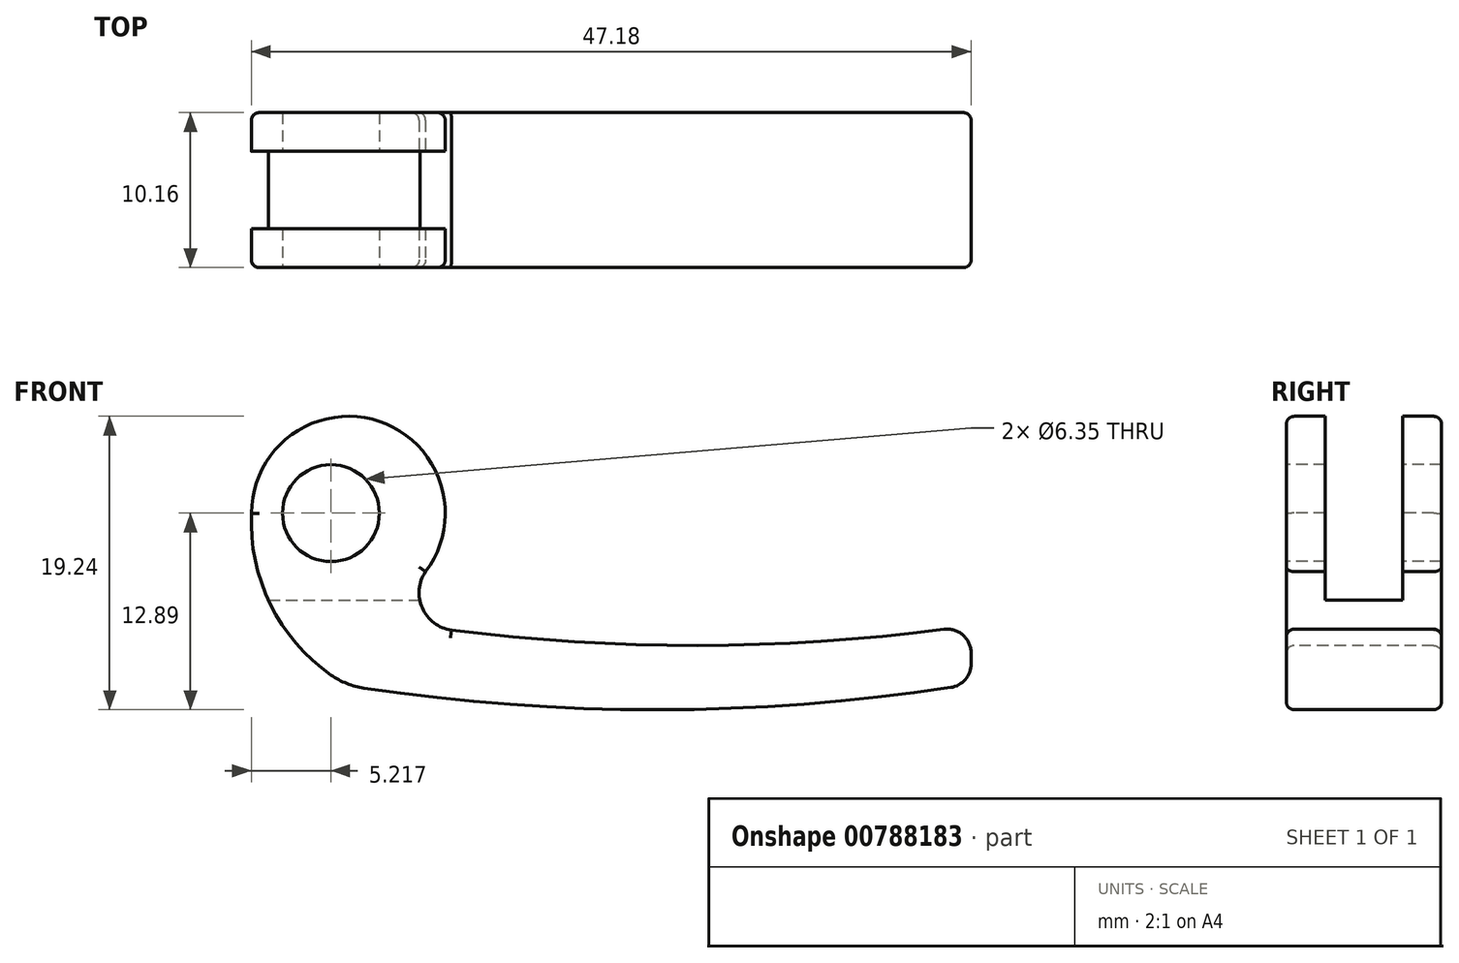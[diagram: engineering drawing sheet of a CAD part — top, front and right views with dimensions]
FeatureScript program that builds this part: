
annotation { "Feature Type Name" : "Feature", "Feature Type Description" : "" }
export const myFeature = defineFeature(function(context is Context, id is Id, definition is map)
    precondition{}
    {
        {
            var Q0;
            Q0=qCreatedBy(makeId("Front.planeOp"),FACE);
            var sketch = newSketch(context, id + "F0", { "sketchPlane" : qUnion([Q0])});
            skArc(sketch, "E0", {"start": v(5.06, -3.84) * mm, "mid": v(2.02, 6.02) * mm, "end": v(-6.35, 0) * mm});
            skCircle(sketch, "E1", {"center": v(-1.14, 0) * mm, "radius": 3.18 * mm});
            skArc(sketch, "E2", {"start": v(0, -11.31) * mm, "mid": v(20.42, -12.89) * mm, "end": v(40.82, -11.22) * mm});
            skArc(sketch, "E3", {"start": v(5.06, -3.84) * mm, "mid": v(4.85, -6.22) * mm, "end": v(6.76, -7.66) * mm});
            skLineSegment(sketch, "E4", {"start": v(40.82, -11.22) * mm, "end": v(40.82, -7.36) * mm});
            skArc(sketch, "E5", {"start": v(-6.35, 0) * mm, "mid": v(-4.8, -6.57) * mm, "end": v(0, -11.31) * mm});
            skPoint(sketch, "E6.end.orphan", {"position": v(-7.62, -12.7) * mm});
            skArc(sketch, "E7.trimOffspring", {"start": v(6.76, -7.66) * mm, "mid": v(23.8, -8.67) * mm, "end": v(40.82, -7.36) * mm});
            skSolve(sketch);
        }
        {
            var Q0;
            Q0=qSketchRegion(id+"F0",true);
            extrude(context, id + "F1", {"entities" : qUnion([Q0]), "oppositeDirection" : true, "depth" : 10.16 * mm});
        }
        {
            var Q0;
            Q0=makeQuery(id+"F1.opExtrude","SWEPT_EDGE",EDGE,{"disambiguationData":[OSD([sQuery(id+"F0.wireOp",EDGE,"E4"),sQuery(id+"F0.wireOp",EDGE,"E7.trimOffspring")])]});
            var Q1;
            Q1=makeQuery(id+"F1.opExtrude","SWEPT_EDGE",EDGE,{"disambiguationData":[OSD([sQuery(id+"F0.wireOp",EDGE,"E2"),sQuery(id+"F0.wireOp",EDGE,"E4")])]});
            fillet(context, id + "F2", {"entities" : qUnion([Q0, Q1]), "radius" : 1.57 * mm, "tangentPropagation" : true, "allowEdgeOverflow" : false});
        }
        {
            var Q0;
            Q0=makeQuery(id+"F1.opExtrude","SWEPT_EDGE",EDGE,{"disambiguationData":[OSD([sQuery(id+"F0.wireOp",EDGE,"E2"),sQuery(id+"F0.wireOp",EDGE,"E5")])]});
            fillet(context, id + "F3", {"entities" : qUnion([Q0]), "radius" : 5.08 * mm, "tangentPropagation" : true, "allowEdgeOverflow" : false});
        }
        {
            var Q0;
            Q0=qCreatedBy(makeId("Right.planeOp"),FACE);
            var sketch = newSketch(context, id + "F4", { "sketchPlane" : qUnion([Q0])});
            skLineSegment(sketch, "E8.bottom", {"start": v(2.54, 7.62) * mm, "end": v(7.62, 7.62) * mm});
            skLineSegment(sketch, "E8.top", {"start": v(2.54, -5.72) * mm, "end": v(7.62, -5.72) * mm});
            skLineSegment(sketch, "E8.left", {"start": v(2.54, 7.62) * mm, "end": v(2.54, -5.72) * mm});
            skLineSegment(sketch, "E8.right", {"start": v(7.62, 7.62) * mm, "end": v(7.62, -5.72) * mm});
            skSolve(sketch);
        }
        {
            var Q0;
            Q0=qSketchRegion(id+"F4",true);
            extrude(context, id + "F5", {"entities" : qUnion([Q0]), "operationType" : NewBodyOperationType.REMOVE, "endBound" : BoundingType.SYMMETRIC, "oppositeDirection" : true, "depth" : 25.4 * mm});
        }
        {
            var Q0;
            Q0=makeQuery(id+"F1.opExtrude","CAP_EDGE",EDGE,{"disambiguationData":[OSD([sQuery(id+"F0.wireOp",EDGE,"E0")])],"isStart":true});
            var Q1;
            Q1=makeQuery(id+"F1.opExtrude","CAP_EDGE",EDGE,{"disambiguationData":[OSD([sQuery(id+"F0.wireOp",EDGE,"E3")])],"isStart":true});
            var Q2;
            Q2=makeQuery(id+"F1.opExtrude","CAP_EDGE",EDGE,{"disambiguationData":[OSD([sQuery(id+"F0.wireOp",EDGE,"E7.trimOffspring")])],"isStart":true});
            var Q3;
            {var subQ0=sQuery(id+"F0.wireOp",EDGE,"E4");var subQ1=sQuery(id+"F0.wireOp",EDGE,"E7.trimOffspring");Q3=makeQuery(id+"F2.opFillet","BLEND_EDGE",EDGE,{"blendedFrom":[makeQuery(id+"F1.opExtrude","SWEPT_EDGE",EDGE,{"disambiguationData":[OSD([subQ0,subQ1])]}),makeQuery(id+"F1.opExtrude","CAP_FACE",FACE,{"disambiguationData":[OSD([sQuery(id+"F0.wireOp",EDGE,"E0"),sQuery(id+"F0.wireOp",EDGE,"E1"),sQuery(id+"F0.wireOp",EDGE,"E2"),sQuery(id+"F0.wireOp",EDGE,"E3"),subQ0,sQuery(id+"F0.wireOp",EDGE,"E5"),subQ1])],"isStart":true})],"blendedInto":[makeQuery(id+"F1.opExtrude","CAP_FACE",FACE,{"disambiguationData":[OSD([sQuery(id+"F0.wireOp",EDGE,"E0"),sQuery(id+"F0.wireOp",EDGE,"E1"),sQuery(id+"F0.wireOp",EDGE,"E2"),sQuery(id+"F0.wireOp",EDGE,"E3"),subQ0,sQuery(id+"F0.wireOp",EDGE,"E5"),subQ1])],"isStart":true})]});}
            var Q4;
            Q4=makeQuery(id+"F1.opExtrude","CAP_EDGE",EDGE,{"disambiguationData":[OSD([sQuery(id+"F0.wireOp",EDGE,"E4")])],"isStart":true});
            var Q5;
            {var subQ0=sQuery(id+"F0.wireOp",EDGE,"E2");var subQ1=sQuery(id+"F0.wireOp",EDGE,"E4");Q5=makeQuery(id+"F2.opFillet","BLEND_EDGE",EDGE,{"blendedFrom":[makeQuery(id+"F1.opExtrude","SWEPT_EDGE",EDGE,{"disambiguationData":[OSD([subQ0,subQ1])]}),makeQuery(id+"F1.opExtrude","CAP_FACE",FACE,{"disambiguationData":[OSD([sQuery(id+"F0.wireOp",EDGE,"E0"),sQuery(id+"F0.wireOp",EDGE,"E1"),subQ0,sQuery(id+"F0.wireOp",EDGE,"E3"),subQ1,sQuery(id+"F0.wireOp",EDGE,"E5"),sQuery(id+"F0.wireOp",EDGE,"E7.trimOffspring")])],"isStart":true})],"blendedInto":[makeQuery(id+"F1.opExtrude","CAP_FACE",FACE,{"disambiguationData":[OSD([sQuery(id+"F0.wireOp",EDGE,"E0"),sQuery(id+"F0.wireOp",EDGE,"E1"),subQ0,sQuery(id+"F0.wireOp",EDGE,"E3"),subQ1,sQuery(id+"F0.wireOp",EDGE,"E5"),sQuery(id+"F0.wireOp",EDGE,"E7.trimOffspring")])],"isStart":true})]});}
            var Q6;
            Q6=makeQuery(id+"F1.opExtrude","CAP_EDGE",EDGE,{"disambiguationData":[OSD([sQuery(id+"F0.wireOp",EDGE,"E2")])],"isStart":true});
            var Q7;
            {var subQ0=sQuery(id+"F0.wireOp",EDGE,"E2");var subQ1=sQuery(id+"F0.wireOp",EDGE,"E5");Q7=makeQuery(id+"F3.opFillet","BLEND_EDGE",EDGE,{"blendedFrom":[makeQuery(id+"F1.opExtrude","SWEPT_EDGE",EDGE,{"disambiguationData":[OSD([subQ0,subQ1])]}),makeQuery(id+"F1.opExtrude","CAP_FACE",FACE,{"disambiguationData":[OSD([sQuery(id+"F0.wireOp",EDGE,"E0"),sQuery(id+"F0.wireOp",EDGE,"E1"),subQ0,sQuery(id+"F0.wireOp",EDGE,"E3"),sQuery(id+"F0.wireOp",EDGE,"E4"),subQ1,sQuery(id+"F0.wireOp",EDGE,"E7.trimOffspring")])],"isStart":true})],"blendedInto":[makeQuery(id+"F1.opExtrude","CAP_FACE",FACE,{"disambiguationData":[OSD([sQuery(id+"F0.wireOp",EDGE,"E0"),sQuery(id+"F0.wireOp",EDGE,"E1"),subQ0,sQuery(id+"F0.wireOp",EDGE,"E3"),sQuery(id+"F0.wireOp",EDGE,"E4"),subQ1,sQuery(id+"F0.wireOp",EDGE,"E7.trimOffspring")])],"isStart":true})]});}
            var Q8;
            Q8=makeQuery(id+"F1.opExtrude","CAP_EDGE",EDGE,{"disambiguationData":[OSD([sQuery(id+"F0.wireOp",EDGE,"E5")])],"isStart":true});
            var Q9;
            Q9=makeQuery(id+"F1.opExtrude","CAP_EDGE",EDGE,{"disambiguationData":[OSD([sQuery(id+"F0.wireOp",EDGE,"E2")])],"isStart":false});
            var Q10;
            {var subQ0=sQuery(id+"F0.wireOp",EDGE,"E2");var subQ1=sQuery(id+"F0.wireOp",EDGE,"E4");Q10=makeQuery(id+"F2.opFillet","BLEND_EDGE",EDGE,{"blendedFrom":[makeQuery(id+"F1.opExtrude","SWEPT_EDGE",EDGE,{"disambiguationData":[OSD([subQ0,subQ1])]}),makeQuery(id+"F1.opExtrude","CAP_FACE",FACE,{"disambiguationData":[OSD([sQuery(id+"F0.wireOp",EDGE,"E0"),sQuery(id+"F0.wireOp",EDGE,"E1"),subQ0,sQuery(id+"F0.wireOp",EDGE,"E3"),subQ1,sQuery(id+"F0.wireOp",EDGE,"E5"),sQuery(id+"F0.wireOp",EDGE,"E7.trimOffspring")])],"isStart":false})],"blendedInto":[makeQuery(id+"F1.opExtrude","CAP_FACE",FACE,{"disambiguationData":[OSD([sQuery(id+"F0.wireOp",EDGE,"E0"),sQuery(id+"F0.wireOp",EDGE,"E1"),subQ0,sQuery(id+"F0.wireOp",EDGE,"E3"),subQ1,sQuery(id+"F0.wireOp",EDGE,"E5"),sQuery(id+"F0.wireOp",EDGE,"E7.trimOffspring")])],"isStart":false})]});}
            var Q11;
            Q11=makeQuery(id+"F1.opExtrude","CAP_EDGE",EDGE,{"disambiguationData":[OSD([sQuery(id+"F0.wireOp",EDGE,"E4")])],"isStart":false});
            var Q12;
            {var subQ0=sQuery(id+"F0.wireOp",EDGE,"E4");var subQ1=sQuery(id+"F0.wireOp",EDGE,"E7.trimOffspring");Q12=makeQuery(id+"F2.opFillet","BLEND_EDGE",EDGE,{"blendedFrom":[makeQuery(id+"F1.opExtrude","SWEPT_EDGE",EDGE,{"disambiguationData":[OSD([subQ0,subQ1])]}),makeQuery(id+"F1.opExtrude","CAP_FACE",FACE,{"disambiguationData":[OSD([sQuery(id+"F0.wireOp",EDGE,"E0"),sQuery(id+"F0.wireOp",EDGE,"E1"),sQuery(id+"F0.wireOp",EDGE,"E2"),sQuery(id+"F0.wireOp",EDGE,"E3"),subQ0,sQuery(id+"F0.wireOp",EDGE,"E5"),subQ1])],"isStart":false})],"blendedInto":[makeQuery(id+"F1.opExtrude","CAP_FACE",FACE,{"disambiguationData":[OSD([sQuery(id+"F0.wireOp",EDGE,"E0"),sQuery(id+"F0.wireOp",EDGE,"E1"),sQuery(id+"F0.wireOp",EDGE,"E2"),sQuery(id+"F0.wireOp",EDGE,"E3"),subQ0,sQuery(id+"F0.wireOp",EDGE,"E5"),subQ1])],"isStart":false})]});}
            var Q13;
            Q13=makeQuery(id+"F1.opExtrude","CAP_EDGE",EDGE,{"disambiguationData":[OSD([sQuery(id+"F0.wireOp",EDGE,"E7.trimOffspring")])],"isStart":false});
            var Q14;
            Q14=makeQuery(id+"F1.opExtrude","CAP_EDGE",EDGE,{"disambiguationData":[OSD([sQuery(id+"F0.wireOp",EDGE,"E3")])],"isStart":false});
            var Q15;
            Q15=makeQuery(id+"F1.opExtrude","CAP_EDGE",EDGE,{"disambiguationData":[OSD([sQuery(id+"F0.wireOp",EDGE,"E0")])],"isStart":false});
            var Q16;
            Q16=makeQuery(id+"F1.opExtrude","CAP_EDGE",EDGE,{"disambiguationData":[OSD([sQuery(id+"F0.wireOp",EDGE,"E5")])],"isStart":false});
            var Q17;
            {var subQ0=sQuery(id+"F0.wireOp",EDGE,"E2");var subQ1=sQuery(id+"F0.wireOp",EDGE,"E5");Q17=makeQuery(id+"F3.opFillet","BLEND_EDGE",EDGE,{"blendedFrom":[makeQuery(id+"F1.opExtrude","SWEPT_EDGE",EDGE,{"disambiguationData":[OSD([subQ0,subQ1])]}),makeQuery(id+"F1.opExtrude","CAP_FACE",FACE,{"disambiguationData":[OSD([sQuery(id+"F0.wireOp",EDGE,"E0"),sQuery(id+"F0.wireOp",EDGE,"E1"),subQ0,sQuery(id+"F0.wireOp",EDGE,"E3"),sQuery(id+"F0.wireOp",EDGE,"E4"),subQ1,sQuery(id+"F0.wireOp",EDGE,"E7.trimOffspring")])],"isStart":false})],"blendedInto":[makeQuery(id+"F1.opExtrude","CAP_FACE",FACE,{"disambiguationData":[OSD([sQuery(id+"F0.wireOp",EDGE,"E0"),sQuery(id+"F0.wireOp",EDGE,"E1"),subQ0,sQuery(id+"F0.wireOp",EDGE,"E3"),sQuery(id+"F0.wireOp",EDGE,"E4"),subQ1,sQuery(id+"F0.wireOp",EDGE,"E7.trimOffspring")])],"isStart":false})]});}
            fillet(context, id + "F6", {"entities" : qUnion([Q0, Q1, Q2, Q3, Q4, Q5, Q6, Q7, Q8, Q9, Q10, Q11, Q12, Q13, Q14, Q15, Q16, Q17]), "radius" : 0.5 * mm, "tangentPropagation" : true, "allowEdgeOverflow" : false});
        }
    });
